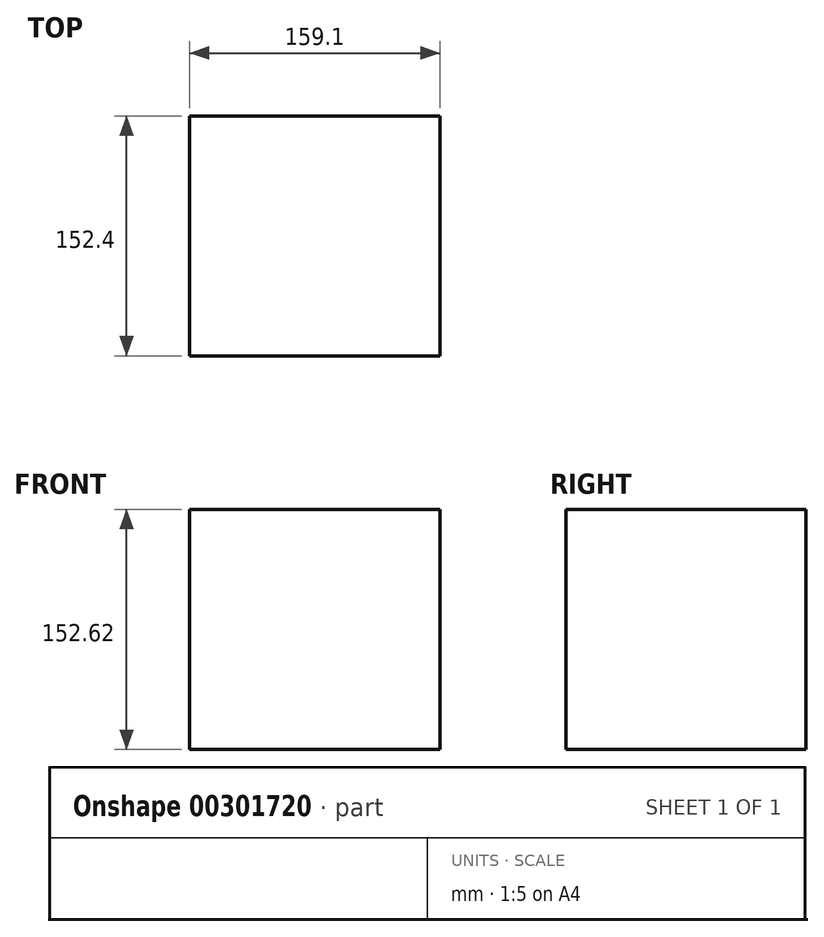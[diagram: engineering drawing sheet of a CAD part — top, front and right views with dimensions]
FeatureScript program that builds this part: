
annotation { "Feature Type Name" : "Feature", "Feature Type Description" : "" }
export const myFeature = defineFeature(function(context is Context, id is Id, definition is map)
    precondition{}
    {
        {
            var Q0;
            Q0=qCreatedBy(makeId("Front.planeOp"),FACE);
            var sketch = newSketch(context, id + "F0", { "sketchPlane" : qUnion([Q0])});
            skLineSegment(sketch, "E0.bottom", {"start": v(79.55, -76.31) * mm, "end": v(-79.55, -76.31) * mm});
            skLineSegment(sketch, "E0.top", {"start": v(79.55, 76.31) * mm, "end": v(-79.55, 76.31) * mm});
            skLineSegment(sketch, "E0.left", {"start": v(79.55, -76.31) * mm, "end": v(79.55, 76.31) * mm});
            skLineSegment(sketch, "E0.right", {"start": v(-79.55, -76.31) * mm, "end": v(-79.55, 76.31) * mm});
            skPoint(sketch, "E0.middle", {"position": v(0, 0) * mm});
            skSolve(sketch);
        }
        {
            var Q0;
            Q0 = qSketchRegion(id + "F0", true);
            extrude(context, id + "F1", {"entities" : qUnion([Q0]), "depth" : 152.4 * mm});
        }
    });
